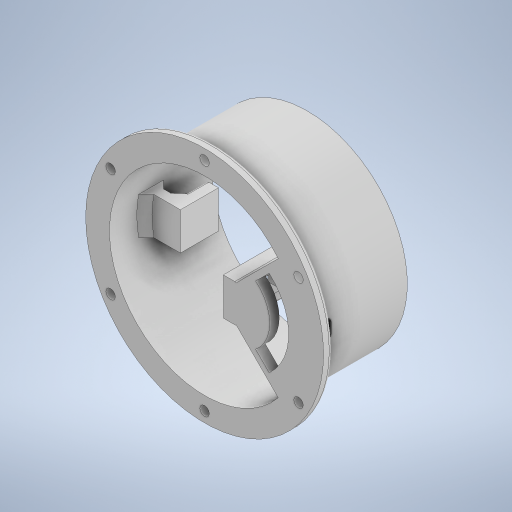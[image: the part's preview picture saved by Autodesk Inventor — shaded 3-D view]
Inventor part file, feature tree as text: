
AUTODESK INVENTOR PART (.ipt)
format: ipt  version: 2024 (Build 280153000, 153)  size: 1,208,320 bytes
history: native  units: mm
features: extrude x15, projected_geometry x10, plane x7, other x7, fillet x5, reference x3, chamfer x2, sketch x1
ambient origin geometry x8: Origin, YZ Plane, XZ Plane, XY Plane, X Axis, Y Axis, Z Axis, Center Point
bodies: Solid1 (feature_tree)
feature tree (50):
  plane  "Work Plane1"
  extrude  "Extrusion1"  Depth=2.0mm
  plane  "Work Plane2"
  plane  "Work Plane3"
  plane  "Work Plane4"
  extrude  "Extrusion3"  Depth=2.0mm
  plane  "Work Plane5"
  extrude  "Extrusion7"  Depth=2.0mm TaperAngle=0.0deg
  extrude  "Extrusion8"  Depth=2.0mm
  extrude  "Extrusion9"  Depth=2.0mm TaperAngle=0.0deg
  chamfer  "Chamfer5"  Distance=15.0mm
  extrude  "Extrusion10"  TaperAngle=45.0deg  [1 undecoded]
  fillet  "Fillet1"  [1 undecoded]
  extrude  "Extrusion11"  Depth=2.0mm
  plane  "Work Plane6"
  extrude  "Extrusion12"  Depth=2.0mm
  chamfer  "Chamfer7"  Distance=4.342145mm
  extrude  "Extrusion13"  Depth=2.0mm
  extrude  "Extrusion14"  Depth=2.0mm
  extrude  "Extrusion15"  Depth=2.0mm
  extrude  "Extrusion16"  Depth=2.0mm TaperAngle=0.0deg
  extrude  "Extrusion17"  Depth=2.0mm TaperAngle=45.0deg
  extrude  "Extrusion18"  Depth=2.0mm
  fillet  "Fillet2"  Radius=36.860536mm
  fillet  "Fillet3"  Radius=6.525mm
  fillet  "Fillet4"  Radius=105.0mm
  plane  "Work Plane7"
  extrude  "Extrusion19"  Depth=2.0mm TaperAngle=0.0deg
  fillet  "Fillet5"  Radius=2.0mm
  reference  "Reference1"
  reference  "Reference2"
  reference  "Reference3"
  projected_geometry  "Projected Loop2"
  projected_geometry  "Projected Loop3"
  projected_geometry  "Projected Loop4"
  sketch  "Sketch11"  dims[d0=15.0mm d1=0.0mm d5=100.0mm d6=105.0mm d7=50.0mm d8=0.0mm d28=9.85mm d30=15.0mm d31=0.0mm d32=15.0mm d33=0.0mm d34=45.0deg d35=45.0deg d36=40.0mm d37=60.0mm d38=4.342145mm d39=9.85mm d40=3.0mm d41=3.0mm d42=5.0mm d43=0.0mm d44=4.0mm d45=2.0mm d46=45.0deg d50=125.0mm d51=36.860536mm d52=6.525mm d53=105.0mm d54=5.0mm d55=0.0mm d56=2.0mm d57=5.0mm d58=57.0mm d59=0.0mm d60=0.0mm d61=60.0mm d63=360.0deg d65=5.0mm d66=10.0mm d67=0.0mm d68=4.0mm d69=2.0mm d70=45.0deg d71=105.0mm d72=100.0mm d73=36.860536mm d74=6.525mm d75=4.0mm d76=0.0mm d77=1.0mm d78=19.7mm d79=1.7mm d80=0.0mm d81=0.0mm d82=2.5mm d83=2.5mm d84=2.5mm d85=2.5mm d86=0.0mm d87=0.0mm d88=2.0mm d89=0.0mm d90=2.0mm d91=0.0mm d93=5.0mm d94=10.0mm d95=0.0mm d96=1.0mm d97=2.0mm d98=2.0mm d99=-83.0mm d100=5.0mm d101=10.0mm d102=0.0mm d103=2.0mm]
  projected_geometry  "Projected Loop5"
  projected_geometry  "Projected Loop6"
  projected_geometry  "Projected Loop7"
  projected_geometry  "Projected Loop8"
  projected_geometry  "Projected Loop9"
  projected_geometry  "Projected Loop10"
  projected_geometry  "Projected Loop11"
  other  "<userpath> windows\Documents\Inventor\Robotska_roka\Assembly4.iam"
  other  "Assembly4.iam"
  other  "Servo Motor MG996R  With Attachments:2"
  other  "servoMotorMG996R_7"
  other  "Servo Motor MG996R  With Attachments:1"
  other  "attachmentCircular_1"
  other  "servoMotorMG996R"
note: 2 required parameter values undecoded (feature->parameter linkage not recoverable at this tier; creation-order binding heuristic only, values carry confidence <= 0.55)
